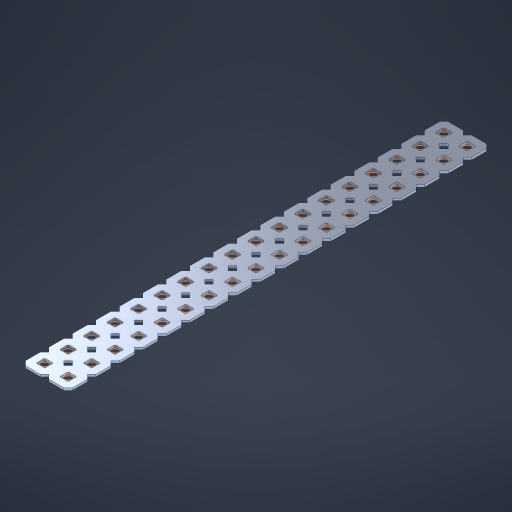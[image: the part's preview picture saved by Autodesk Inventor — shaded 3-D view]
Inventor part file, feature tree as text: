
AUTODESK INVENTOR PART (.ipt)
format: ipt  version: 2023 (Build 270158000, 158)  size: 671,744 bytes
history: native  units: in
note: dims shown in document units (in); Inventor stores cm internally (conversion verified against a paired STEP export)
features: other x37, extrude x35, sketch x2, pattern_linear x1
ambient origin geometry x8: Origin, YZ Plane, XZ Plane, XY Plane, X Axis, Y Axis, Z Axis, Center Point
bodies: Solid1 (feature_tree), Body (feature_tree)
feature tree (75):
  pattern_linear  "Rectangular Pattern1"  Spacing1=0.09in  [1 undecoded]
  sketch  "Sketch1"  dims[d1=0.5in]
  sketch  "Sketch2"  dims[d2=0.182in d3=0.09in d4=0.09in d5=0.09in d6=0.09in d7=0.09in d8=0.09in d9=0.09in d10=0.09in d11=0.02in d13=0.0in d14=0.172in d15=0.0625in d16=0.0in d19=0.5in d22=0.5in]
  other  "Srf1"
  other  "Srf126"
  other  "Srf127"
  other  "Srf128"
  other  "Srf129"
  other  "Srf130"
  other  "Srf131"
  other  "Srf250"
  other  "Srf251"
  other  "Srf252"
  other  "Srf253"
  other  "Srf254"
  other  "Srf255"
  other  "Srf256"
  other  "Srf257"
  other  "Srf258"
  other  "Srf259"
  other  "Srf260"
  other  "Srf268"
  other  "Srf269"
  other  "Srf270"
  other  "Srf271"
  other  "Srf272"
  other  "Srf273"
  other  "Srf274"
  other  "Srf275"
  other  "Srf276"
  other  "Srf277"
  other  "Srf278"
  other  "Srf279"
  other  "Srf280"
  other  "Srf281"
  other  "Srf282"
  other  "Srf283"
  other  "Srf284"
  other  "Srf285"
  other  "Circle"
  extrude  "ExtrusionSrf126"  Depth=0.09in
  extrude  "ExtrusionSrf127"  Depth=0.09in
  extrude  "ExtrusionSrf128"  Depth=0.09in
  extrude  "ExtrusionSrf129"  Depth=0.09in
  extrude  "ExtrusionSrf130"  Depth=0.09in
  extrude  "ExtrusionSrf131"  Depth=0.09in
  extrude  "ExtrusionSrf250"  Depth=0.09in
  extrude  "ExtrusionSrf251"  Depth=0.02in
  extrude  "ExtrusionSrf252"  TaperAngle=0.0deg  [1 undecoded]
  extrude  "ExtrusionSrf253"  Depth=0.5in
  extrude  "ExtrusionSrf254"  Depth=0.5in TaperAngle=0.0deg
  extrude  "ExtrusionSrf255"  Depth=0.5in
  extrude  "ExtrusionSrf256"  Depth=0.5in
  extrude  "ExtrusionSrf257"  [1 undecoded]
  extrude  "ExtrusionSrf258"  [1 undecoded]
  extrude  "ExtrusionSrf259"  [1 undecoded]
  extrude  "ExtrusionSrf260"  [1 undecoded]
  extrude  "ExtrusionSrf268"  [1 undecoded]
  extrude  "ExtrusionSrf269"  [1 undecoded]
  extrude  "ExtrusionSrf270"  [1 undecoded]
  extrude  "ExtrusionSrf271"  [1 undecoded]
  extrude  "ExtrusionSrf272"  [1 undecoded]
  extrude  "ExtrusionSrf273"  [1 undecoded]
  extrude  "ExtrusionSrf274"  [1 undecoded]
  extrude  "ExtrusionSrf275"  [1 undecoded]
  extrude  "ExtrusionSrf276"  [1 undecoded]
  extrude  "ExtrusionSrf277"  [1 undecoded]
  extrude  "ExtrusionSrf278"  [1 undecoded]
  extrude  "ExtrusionSrf279"  [1 undecoded]
  extrude  "ExtrusionSrf280"  [1 undecoded]
  extrude  "ExtrusionSrf281"  [1 undecoded]
  extrude  "ExtrusionSrf282"  [1 undecoded]
  extrude  "ExtrusionSrf283"  [1 undecoded]
  extrude  "ExtrusionSrf284"  [1 undecoded]
  extrude  "ExtrusionSrf285"  [1 undecoded]
note: 24 required parameter values undecoded (feature->parameter linkage not recoverable at this tier; creation-order binding heuristic only, values carry confidence <= 0.55)
